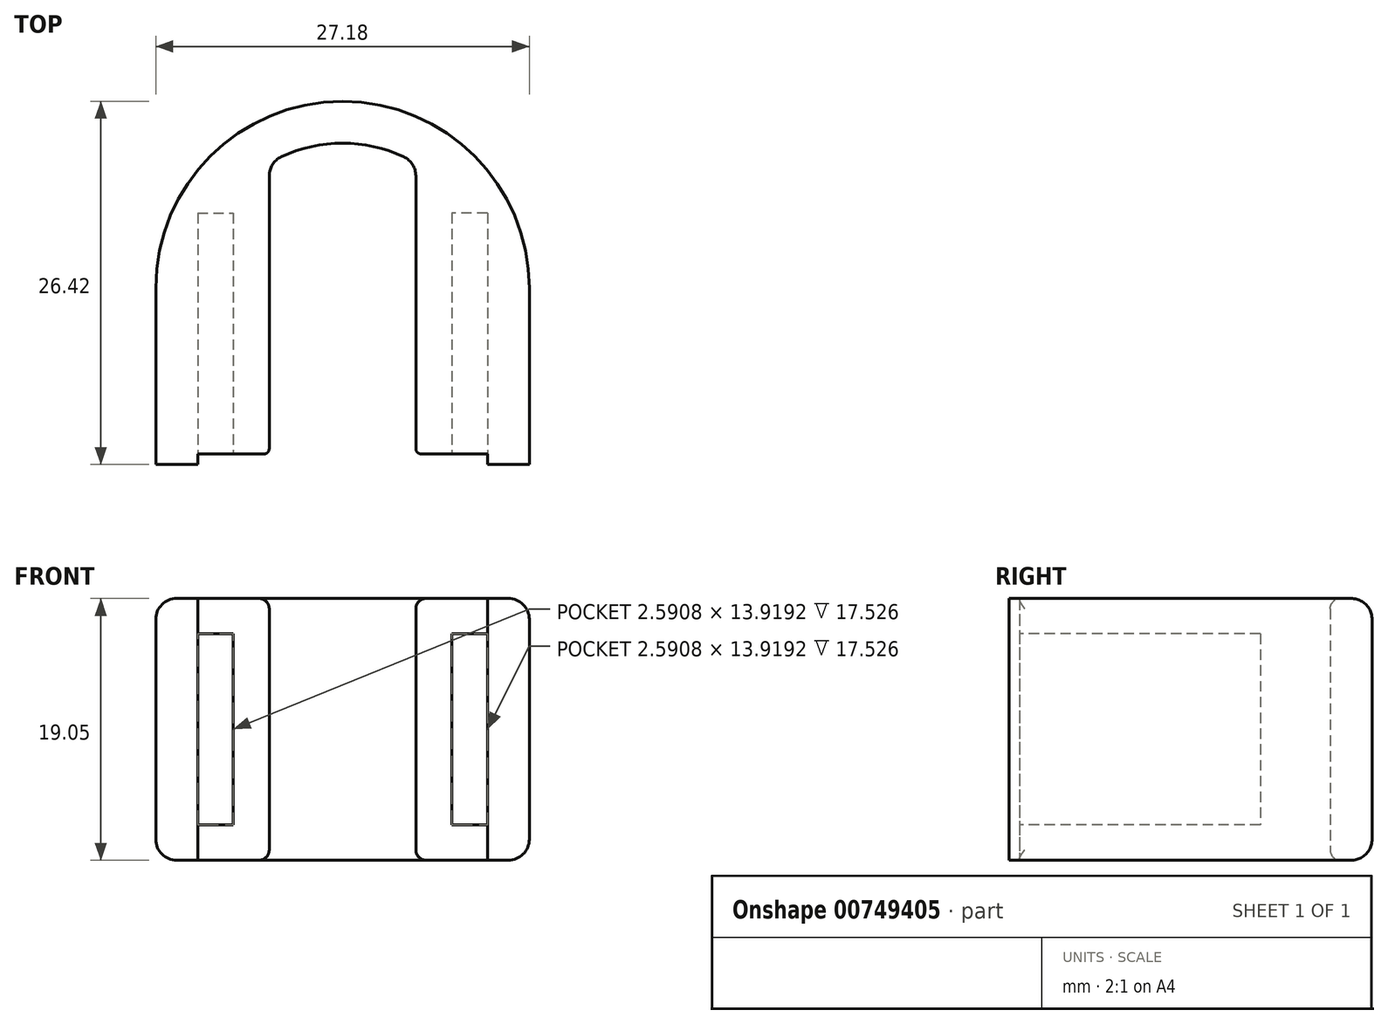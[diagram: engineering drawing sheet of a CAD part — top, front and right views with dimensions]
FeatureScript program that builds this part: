
annotation { "Feature Type Name" : "Feature", "Feature Type Description" : "" }
export const myFeature = defineFeature(function(context is Context, id is Id, definition is map)
    precondition{}
    {
        {
            var Q0;
            Q0=qCreatedBy(makeId("Top.planeOp"),FACE);
            var sketch = newSketch(context, id + "F0", { "sketchPlane" : qUnion([Q0])});
            skArc(sketch, "E0", {"start": v(13.59, 0) * mm, "mid": v(0, 13.59) * mm, "end": v(-13.59, 0) * mm});
            skLineSegment(sketch, "E1", {"start": v(0, 0) * mm, "end": v(0, -35.92) * mm, "construction": true});
            skLineSegment(sketch, "E2", {"start": v(13.59, 0) * mm, "end": v(13.59, -12.83) * mm});
            skLineSegment(sketch, "E3", {"start": v(13.59, 0) * mm, "end": v(-20.52, 0) * mm, "construction": true});
            skLineSegment(sketch, "E4", {"start": v(-13.59, 0) * mm, "end": v(-13.59, -12.83) * mm});
            skLineSegment(sketch, "E5", {"start": v(0, 13.59) * mm, "end": v(29.1, 13.59) * mm, "construction": true});
            skLineSegment(sketch, "E6.0", {"start": v(-13.59, -12.83) * mm, "end": v(-10.54, -12.83) * mm});
            skLineSegment(sketch, "E7.0", {"start": v(-5.33, 8.17) * mm, "end": v(-5.33, -11.68) * mm});
            skLineSegment(sketch, "E8.0", {"start": v(5.33, 8.17) * mm, "end": v(5.33, -11.68) * mm});
            skArc(sketch, "E9.0", {"start": v(4.45, 9.55) * mm, "mid": v(0, 10.54) * mm, "end": v(-4.45, 9.55) * mm});
            skPoint(sketch, "E10.visualSharp", {"position": v(-5.33, 9.1) * mm});
            skArc(sketch, "E10.filletArc", {"start": v(-4.45, 9.55) * mm, "mid": v(-5.1, 9) * mm, "end": v(-5.33, 8.17) * mm});
            skPoint(sketch, "E11.visualSharp", {"position": v(5.33, 9.1) * mm});
            skArc(sketch, "E11.filletArc", {"start": v(5.33, 8.17) * mm, "mid": v(5.1, 9) * mm, "end": v(4.45, 9.55) * mm});
            skLineSegment(sketch, "E12.trimOffspring", {"start": v(10.54, -12.83) * mm, "end": v(13.59, -12.83) * mm});
            skLineSegment(sketch, "E13.0", {"start": v(-10.54, -12.06) * mm, "end": v(-10.54, -12.83) * mm});
            skLineSegment(sketch, "E14.0", {"start": v(10.54, -12.06) * mm, "end": v(10.54, -12.83) * mm});
            skLineSegment(sketch, "E15.0", {"start": v(-10.54, -12.06) * mm, "end": v(-5.72, -12.06) * mm});
            skLineSegment(sketch, "E16.0", {"start": v(5.71, -12.06) * mm, "end": v(10.54, -12.06) * mm});
            skPoint(sketch, "E17.visualSharp", {"position": v(-5.33, -12.06) * mm});
            skArc(sketch, "E17.filletArc", {"start": v(-5.72, -12.06) * mm, "mid": v(-5.45, -11.95) * mm, "end": v(-5.33, -11.68) * mm});
            skPoint(sketch, "E18.visualSharp", {"position": v(5.33, -12.06) * mm});
            skArc(sketch, "E18.filletArc", {"start": v(5.33, -11.68) * mm, "mid": v(5.45, -11.95) * mm, "end": v(5.71, -12.06) * mm});
            skSolve(sketch);
        }
        {
            var Q0;
            Q0=makeQuery(id+"F0.imprint","IMPRINT",FACE,{"disambiguationData":[TD([[makeQuery(id+"F0.imprint","IMPRINT",EDGE,{"derivedFrom":sQuery(id+"F0.wireOp",EDGE,"E0")}),1.0]])]});
            extrude(context, id + "F1", {"entities" : qUnion([Q0]), "depth" : 19.05 * mm, "offsetDistance" : 25.4 * mm});
        }
        {
            var Q0;
            Q0=makeQuery(id+"F1.opExtrude","SWEPT_FACE",FACE,{"disambiguationData":[OSD([sQuery(id+"F0.wireOp",EDGE,"E15.0")])]});
            var sketch = newSketch(context, id + "F2", { "sketchPlane" : qUnion([Q0])});
            skLineSegment(sketch, "E19.bottom", {"start": v(-10.54, 16.48) * mm, "end": v(-7.95, 16.48) * mm});
            skLineSegment(sketch, "E19.top", {"start": v(-10.54, 2.57) * mm, "end": v(-7.95, 2.57) * mm});
            skLineSegment(sketch, "E19.left", {"start": v(-10.54, 16.48) * mm, "end": v(-10.54, 2.57) * mm});
            skLineSegment(sketch, "E19.right", {"start": v(-7.95, 16.48) * mm, "end": v(-7.95, 2.57) * mm});
            skPoint(sketch, "E19.middle", {"position": v(-9.24, 9.53) * mm});
            skPoint(sketch, "E19.middle.positionSnap0", {"position": v(-10.54, 9.53) * mm});
            skPoint(sketch, "E19.centerSnap0", {"position": v(-10.54, 9.53) * mm});
            skSolve(sketch);
        }
        {
            var Q0;
            Q0=makeQuery(id+"F2.imprint","IMPRINT",FACE,{"disambiguationData":[TD([[makeQuery(id+"F2.imprint","IMPRINT",EDGE,{"derivedFrom":sQuery(id+"F2.wireOp",EDGE,"E19.bottom")}),-1.0]])]});
            extrude(context, id + "F3", {"entities" : qUnion([Q0]), "operationType" : NewBodyOperationType.REMOVE, "oppositeDirection" : true, "depth" : 17.53 * mm, "offsetDistance" : 25.4 * mm});
        }
        {
            var Q0;
            Q0=makeQuery(id+"F1.opExtrude","SWEPT_FACE",FACE,{"disambiguationData":[OSD([sQuery(id+"F0.wireOp",EDGE,"E16.0")])]});
            var sketch = newSketch(context, id + "F4", { "sketchPlane" : qUnion([Q0])});
            skLineSegment(sketch, "E20.bottom", {"start": v(10.54, 16.48) * mm, "end": v(7.95, 16.48) * mm});
            skLineSegment(sketch, "E20.top", {"start": v(10.54, 2.57) * mm, "end": v(7.95, 2.57) * mm});
            skLineSegment(sketch, "E20.left", {"start": v(10.54, 16.48) * mm, "end": v(10.54, 2.57) * mm});
            skLineSegment(sketch, "E20.right", {"start": v(7.95, 16.48) * mm, "end": v(7.95, 2.57) * mm});
            skPoint(sketch, "E20.middle", {"position": v(9.25, 9.53) * mm});
            skSolve(sketch);
        }
        {
            var Q0;
            Q0=makeQuery(id+"F4.imprint","IMPRINT",FACE,{"disambiguationData":[TD([[makeQuery(id+"F4.imprint","IMPRINT",EDGE,{"derivedFrom":sQuery(id+"F4.wireOp",EDGE,"E20.bottom")}),1.0]])]});
            extrude(context, id + "F5", {"entities" : qUnion([Q0]), "operationType" : NewBodyOperationType.REMOVE, "oppositeDirection" : true, "depth" : 17.53 * mm, "offsetDistance" : 25.4 * mm});
        }
        {
            var Q0;
            Q0=makeQuery(id+"F1.opExtrude","CAP_EDGE",EDGE,{"disambiguationData":[OSD([sQuery(id+"F0.wireOp",EDGE,"E2")])],"isStart":false});
            var Q1;
            Q1=makeQuery(id+"F1.opExtrude","CAP_EDGE",EDGE,{"disambiguationData":[OSD([sQuery(id+"F0.wireOp",EDGE,"E2")])],"isStart":true});
            fillet(context, id + "F6", {"entities" : qUnion([Q0, Q1]), "radius" : 1.52 * mm, "tangentPropagation" : true, "allowEdgeOverflow" : false});
        }
        {
            var Q0;
            Q0=makeQuery(id+"F1.opExtrude","CAP_EDGE",EDGE,{"disambiguationData":[OSD([sQuery(id+"F0.wireOp",EDGE,"E7.0")])],"isStart":false});
            var Q1;
            Q1=makeQuery(id+"F1.opExtrude","CAP_EDGE",EDGE,{"disambiguationData":[OSD([sQuery(id+"F0.wireOp",EDGE,"E10.filletArc")])],"isStart":false});
            var Q2;
            Q2=makeQuery(id+"F1.opExtrude","CAP_EDGE",EDGE,{"disambiguationData":[OSD([sQuery(id+"F0.wireOp",EDGE,"E9.0")])],"isStart":false});
            var Q3;
            Q3=makeQuery(id+"F1.opExtrude","CAP_EDGE",EDGE,{"disambiguationData":[OSD([sQuery(id+"F0.wireOp",EDGE,"E11.filletArc")])],"isStart":false});
            var Q4;
            Q4=makeQuery(id+"F1.opExtrude","CAP_EDGE",EDGE,{"disambiguationData":[OSD([sQuery(id+"F0.wireOp",EDGE,"E8.0")])],"isStart":false});
            var Q5;
            Q5=makeQuery(id+"F1.opExtrude","CAP_EDGE",EDGE,{"disambiguationData":[OSD([sQuery(id+"F0.wireOp",EDGE,"E8.0")])],"isStart":true});
            var Q6;
            Q6=makeQuery(id+"F1.opExtrude","CAP_EDGE",EDGE,{"disambiguationData":[OSD([sQuery(id+"F0.wireOp",EDGE,"E11.filletArc")])],"isStart":true});
            var Q7;
            Q7=makeQuery(id+"F1.opExtrude","CAP_EDGE",EDGE,{"disambiguationData":[OSD([sQuery(id+"F0.wireOp",EDGE,"E9.0")])],"isStart":true});
            var Q8;
            Q8=makeQuery(id+"F1.opExtrude","CAP_EDGE",EDGE,{"disambiguationData":[OSD([sQuery(id+"F0.wireOp",EDGE,"E10.filletArc")])],"isStart":true});
            var Q9;
            Q9=makeQuery(id+"F1.opExtrude","CAP_EDGE",EDGE,{"disambiguationData":[OSD([sQuery(id+"F0.wireOp",EDGE,"E7.0")])],"isStart":true});
            fillet(context, id + "F7", {"entities" : qUnion([Q0, Q1, Q2, Q3, Q4, Q5, Q6, Q7, Q8, Q9]), "radius" : 0.76 * mm, "allowEdgeOverflow" : false});
        }
    });
